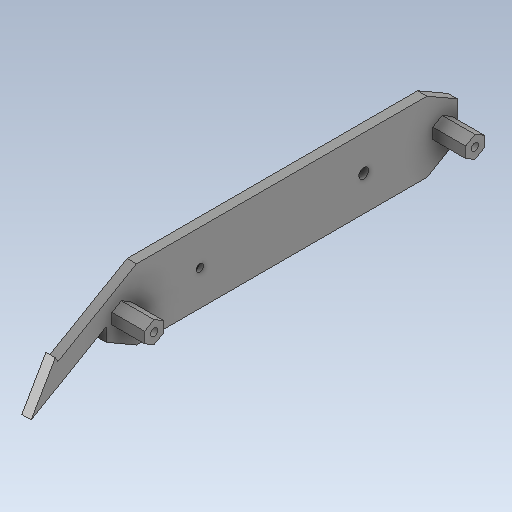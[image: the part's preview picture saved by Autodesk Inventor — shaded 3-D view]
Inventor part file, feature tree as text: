
AUTODESK INVENTOR PART (.ipt)
format: ipt  version: 2020 (Build 240168000, 168)  size: 166,400 bytes
history: native  units: in
note: dims shown in document units (in); Inventor stores cm internally (conversion verified against a paired STEP export)
features: other x3, extrude x1, sketch x1
ambient origin geometry x8: Origin, YZ Plane, XZ Plane, XY Plane, X Axis, Y Axis, Z Axis, Center Point
bodies: Solid1 (feature_tree)
feature tree (5):
  other  "HexWheelGuard.ipt"
  extrude  "Extrusion1"  TaperAngle=0.0deg  [1 undecoded]
  other  "Solid1::HexWheelGuard.ipt"
  other  "TaggingFeature1"
  sketch  "Sketch1"  dims[d0=0.3937in d6=0.0in d7=0.0in d9=0.315in d10=1.3858in d11=60.0deg d12=0.0787in]
note: 1 required parameter value undecoded (feature->parameter linkage not recoverable at this tier; creation-order binding heuristic only, values carry confidence <= 0.55)
